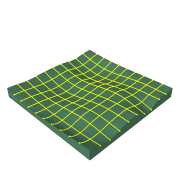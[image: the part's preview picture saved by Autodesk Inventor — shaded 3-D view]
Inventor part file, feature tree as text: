
AUTODESK INVENTOR PART (.ipt)
format: ipt  version: 2021 (Build 250183000, 183)  size: 2,477,056 bytes
history: native  units: in
note: dims shown in document units (in); Inventor stores cm internally (conversion verified against a paired STEP export)
features: sketch x12, projected_geometry x11, extrude x6, plane x3, fillet x1, loft x1, other x1
ambient origin geometry x8: Origin, YZ Plane, XZ Plane, XY Plane, X Axis, Y Axis, Z Axis, Center Point
bodies: Solid1 (feature_tree)
feature tree (35):
  extrude  "Extrusion1"  Depth=3937.0079in
  extrude  "Extrusion2"  Depth=157.4803in
  fillet  "Fillet1"  Radius=393.7008in
  extrude  "Extrusion3"  Depth=118.1102in TaperAngle=0.0deg
  extrude  "Extrusion4"  [1 undecoded]
  sketch  "Sketch5"  dims[d25=-3052.3125in d26=0.0in d27=90.0deg]
  sketch  "Sketch6"  dims[d28=0.0in d29=90.0deg d30=0.0in d31=90.0deg]
  plane  "Work Plane1"
  sketch  "Sketch7"  dims[d32=0.0in d33=90.0deg d34=590.5512in d35=0.0in]
  plane  "Work Plane2"
  loft  "Loft3"
  extrude  "Extrusion6"  TaperAngle=0.0deg  [1 undecoded]
  extrude  "Extrusion7"  Depth=590.5512in TaperAngle=0.0deg
  plane  "Work Plane3"
  sketch  "Sketch11"  dims[d40=3.5433in d42=393.7008in d43=0.3937in d45=1.0in d47=393.7008in d48=3.5433in d50=393.7008in d51=0.3937in d53=1.0in]
  sketch  "3D Sketch2"
  sketch  "Sketch1"  dims[d0=3937.0079in d1=3937.0079in]
  sketch  "Sketch2"  dims[d2=393.7008in d3=0.0in d4=157.4803in d5=393.7008in d6=0.0in]
  projected_geometry  "Projected Loop1"
  sketch  "Sketch3"  dims[d7=19.685in d8=118.1102in d9=0.0in]
  projected_geometry  "Projected Loop2"
  sketch  "Sketch4"  dims[d10=1.0in d11=0.0in d18=-808.3125in]
  projected_geometry  "Projected Loop3"
  projected_geometry  "Projected Loop4"
  projected_geometry  "Projected Loop5"
  projected_geometry  "Projected Loop6"
  sketch  "Sketch8"  dims[d36=196.8504in d37=0.0in]
  sketch  "Sketch9"  dims[d38=-1689.875in]
  sketch  "Sketch10"  dims[d39=393.7008in]
  projected_geometry  "Projected Loop7"
  projected_geometry  "Projected Loop8"
  projected_geometry  "Projected Loop9"
  projected_geometry  "Projected Loop10"
  projected_geometry  "Projected Loop11"
  other  "Project to Surface2"
note: 2 required parameter values undecoded (feature->parameter linkage not recoverable at this tier; creation-order binding heuristic only, values carry confidence <= 0.55)
